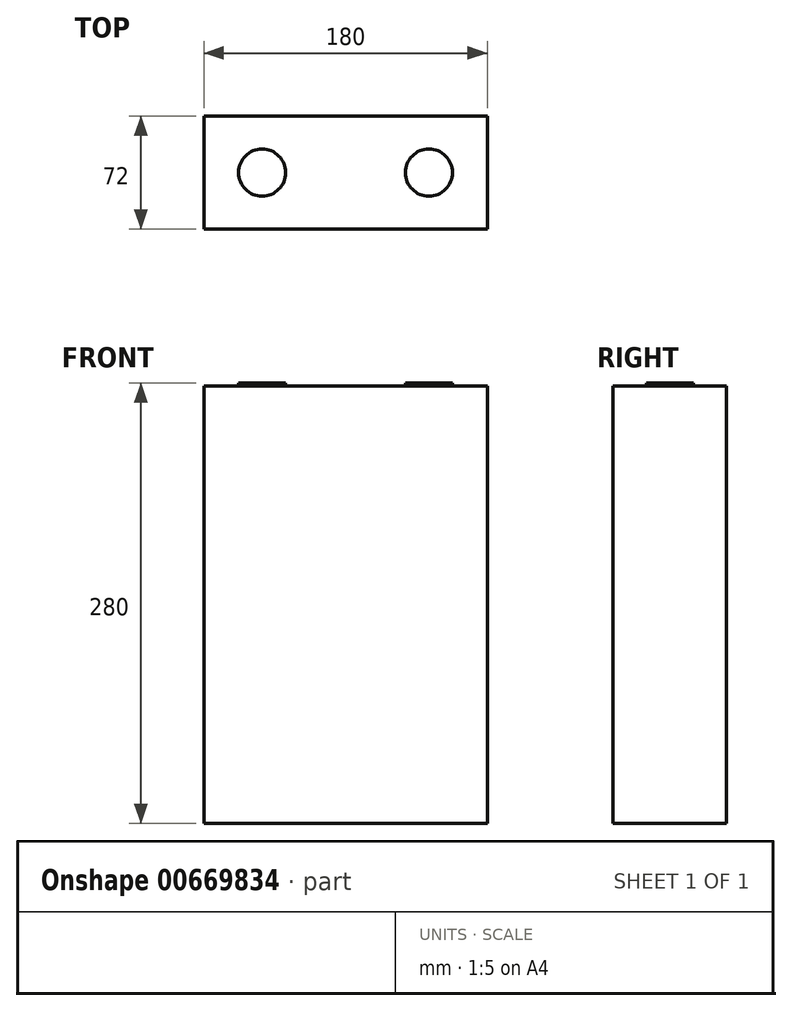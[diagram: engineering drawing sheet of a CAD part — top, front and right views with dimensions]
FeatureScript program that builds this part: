
annotation { "Feature Type Name" : "Feature", "Feature Type Description" : "" }
export const myFeature = defineFeature(function(context is Context, id is Id, definition is map)
    precondition{}
    {
        {
            var Q0;
            Q0=qCreatedBy(makeId("Front.planeOp"),FACE);
            var sketch = newSketch(context, id + "F0", { "sketchPlane" : qUnion([Q0])});
            skLineSegment(sketch, "E0.bottom", {"start": v(-90, 0) * mm, "end": v(90, 0) * mm});
            skLineSegment(sketch, "E0.top", {"start": v(-90, 278) * mm, "end": v(90, 278) * mm});
            skLineSegment(sketch, "E0.left", {"start": v(-90, 0) * mm, "end": v(-90, 278) * mm});
            skLineSegment(sketch, "E0.right", {"start": v(90, 0) * mm, "end": v(90, 278) * mm});
            skSolve(sketch);
        }
        {
            var Q0;
            Q0 = qSketchRegion(id + "F0", true);
            extrude(context, id + "F1", {"entities" : qUnion([Q0]), "endBound" : BoundingType.SYMMETRIC, "depth" : 72 * mm, "offsetDistance" : 25.4 * mm});
        }
        {
            var Q0;
            Q0=qCreatedBy(makeId("Top.planeOp"),FACE);
            var sketch = newSketch(context, id + "F2", { "sketchPlane" : qUnion([Q0])});
            skLineSegment(sketch, "E1", {"start": v(-53, 0) * mm, "end": v(53, 0) * mm, "construction": true});
            skCircle(sketch, "E2", {"center": v(-53, 0) * mm, "radius": 15 * mm});
            skCircle(sketch, "E3", {"center": v(53, 0) * mm, "radius": 15 * mm});
            skSolve(sketch);
        }
        {
            var Q0;
            Q0 = qSketchRegion(id + "F2", true);
            extrude(context, id + "F3", {"entities" : qUnion([Q0]), "operationType" : NewBodyOperationType.ADD, "depth" : 280 * mm, "offsetDistance" : 25 * mm});
        }
    });
